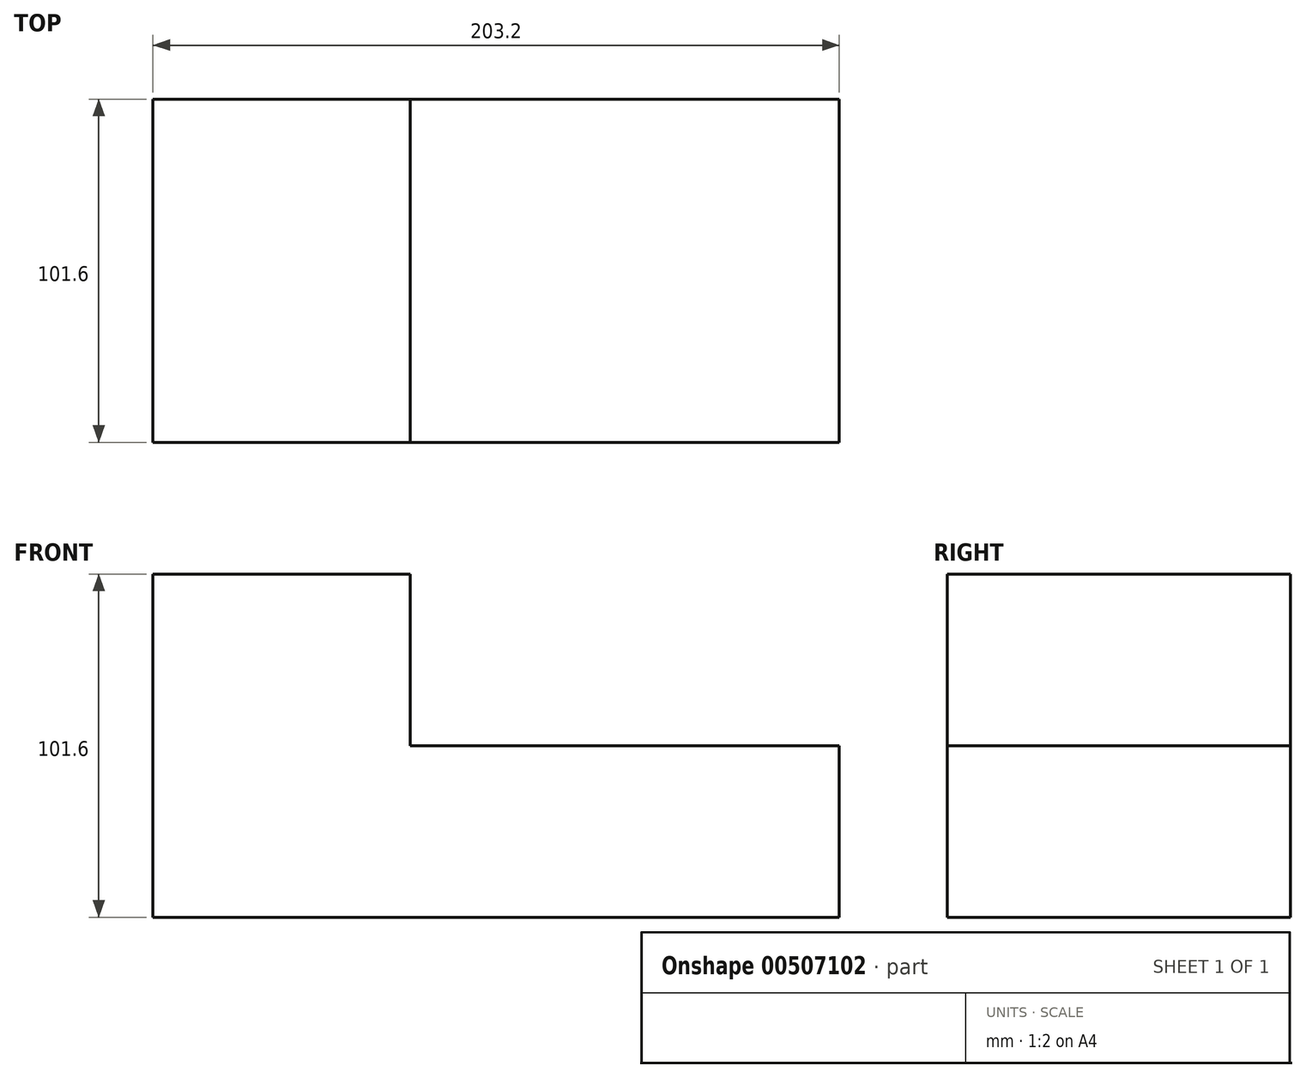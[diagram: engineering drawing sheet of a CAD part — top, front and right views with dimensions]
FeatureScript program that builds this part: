
annotation { "Feature Type Name" : "Feature", "Feature Type Description" : "" }
export const myFeature = defineFeature(function(context is Context, id is Id, definition is map)
    precondition{}
    {
        {
            var Q0;
            Q0=qCreatedBy(makeId("Front.planeOp"),FACE);
            var sketch = newSketch(context, id + "F0", { "sketchPlane" : qUnion([Q0])});
            skLineSegment(sketch, "E0", {"start": v(0, 0) * mm, "end": v(-203.2, 0) * mm});
            skLineSegment(sketch, "E1", {"start": v(-203.2, 0) * mm, "end": v(-203.2, 101.6) * mm});
            skLineSegment(sketch, "E2", {"start": v(0, 0) * mm, "end": v(0, 50.8) * mm});
            skLineSegment(sketch, "E3", {"start": v(0, 50.8) * mm, "end": v(-127, 50.8) * mm});
            skLineSegment(sketch, "E4", {"start": v(-127, 50.8) * mm, "end": v(-127, 101.6) * mm});
            skLineSegment(sketch, "E5", {"start": v(-127, 101.6) * mm, "end": v(-203.2, 101.6) * mm});
            skSolve(sketch);
        }
        {
            var Q0;
            Q0=makeQuery(id+"F0.imprint","IMPRINT",FACE,{"disambiguationData":[TD([[makeQuery(id+"F0.imprint","IMPRINT",EDGE,{"derivedFrom":sQuery(id+"F0.wireOp",EDGE,"E0")}),-1.0]])]});
            extrude(context, id + "F1", {"entities" : qUnion([Q0]), "depth" : 101.6 * mm});
        }
    });
